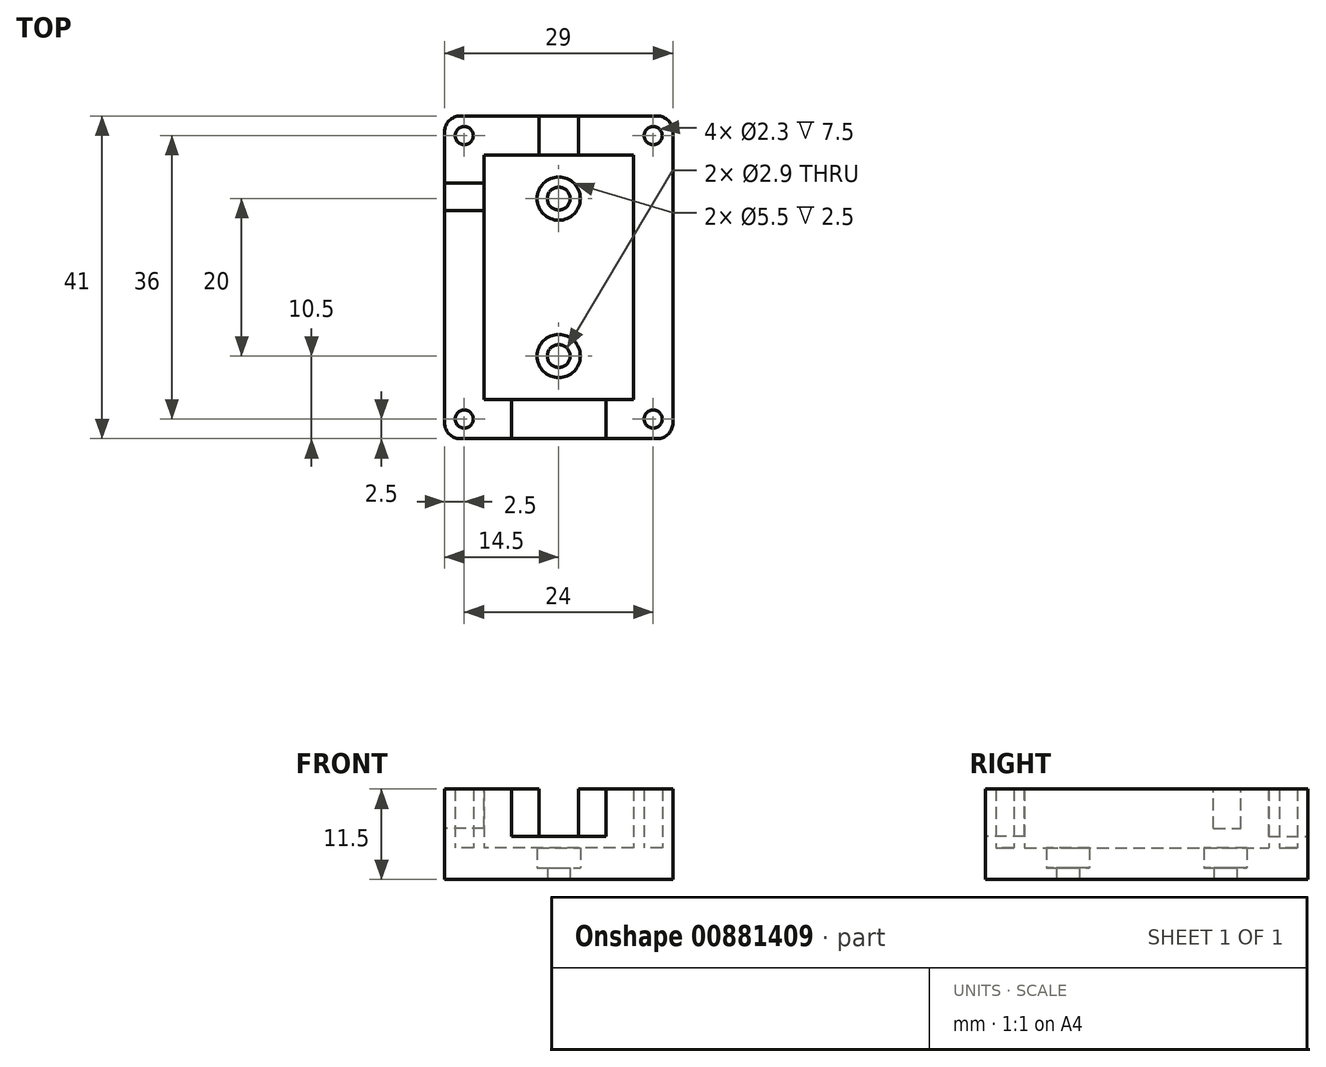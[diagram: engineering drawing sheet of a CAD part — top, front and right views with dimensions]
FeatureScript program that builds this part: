
annotation { "Feature Type Name" : "Feature", "Feature Type Description" : "" }
export const myFeature = defineFeature(function(context is Context, id is Id, definition is map)
    precondition{}
    {
        {
            var Q0;
            Q0=qCreatedBy(makeId("Top.planeOp"),FACE);
            var sketch = newSketch(context, id + "F0", { "sketchPlane" : qUnion([Q0])});
            skLineSegment(sketch, "E0.bottom", {"start": v(9.5, -15.5) * mm, "end": v(-9.5, -15.5) * mm});
            skLineSegment(sketch, "E0.top", {"start": v(9.5, 15.5) * mm, "end": v(-9.5, 15.5) * mm});
            skLineSegment(sketch, "E0.left", {"start": v(9.5, -15.5) * mm, "end": v(9.5, 15.5) * mm});
            skLineSegment(sketch, "E0.right", {"start": v(-9.5, -15.5) * mm, "end": v(-9.5, 15.5) * mm});
            skPoint(sketch, "E0.middle", {"position": v(0, 0) * mm});
            skLineSegment(sketch, "E1.0", {"start": v(14.5, 20.5) * mm, "end": v(-14.5, 20.5) * mm});
            skLineSegment(sketch, "E1.1", {"start": v(14.5, -20.5) * mm, "end": v(14.5, 20.5) * mm});
            skLineSegment(sketch, "E1.2", {"start": v(14.5, -20.5) * mm, "end": v(-14.5, -20.5) * mm});
            skLineSegment(sketch, "E1.3", {"start": v(-14.5, -20.5) * mm, "end": v(-14.5, 20.5) * mm});
            skPoint(sketch, "E2", {"position": v(12, 18) * mm});
            skPoint(sketch, "E3", {"position": v(-12, 18) * mm});
            skPoint(sketch, "E4", {"position": v(-12, -18) * mm});
            skPoint(sketch, "E5", {"position": v(12, -18) * mm});
            skCircle(sketch, "E6", {"center": v(-12, -18) * mm, "radius": 1.15 * mm});
            skCircle(sketch, "E7", {"center": v(12, -18) * mm, "radius": 1.15 * mm});
            skCircle(sketch, "E8", {"center": v(12, 18) * mm, "radius": 1.15 * mm});
            skCircle(sketch, "E9", {"center": v(-12, 18) * mm, "radius": 1.15 * mm});
            skSolve(sketch);
        }
        {
            var Q0;
            Q0=makeQuery(id+"F0.imprint","IMPRINT",FACE,{"disambiguationData":[TD([[makeQuery(id+"F0.imprint","IMPRINT",EDGE,{"derivedFrom":sQuery(id+"F0.wireOp",EDGE,"E0.bottom")}),1.0]])]});
            extrude(context, id + "F1", {"entities" : qUnion([Q0]), "depth" : 7.5 * mm, "offsetDistance" : 25 * mm});
        }
        {
            var Q0;
            Q0=makeQuery(id+"F1.opExtrude","CAP_FACE",FACE,{"disambiguationData":[OSD([sQuery(id+"F0.wireOp",EDGE,"E0.bottom"),sQuery(id+"F0.wireOp",EDGE,"E0.top"),sQuery(id+"F0.wireOp",EDGE,"E0.left"),sQuery(id+"F0.wireOp",EDGE,"E0.right"),sQuery(id+"F0.wireOp",EDGE,"E1.0"),sQuery(id+"F0.wireOp",EDGE,"E1.1"),sQuery(id+"F0.wireOp",EDGE,"E1.2"),sQuery(id+"F0.wireOp",EDGE,"E1.3"),sQuery(id+"F0.wireOp",EDGE,"E6"),sQuery(id+"F0.wireOp",EDGE,"E7"),sQuery(id+"F0.wireOp",EDGE,"E8"),sQuery(id+"F0.wireOp",EDGE,"E9")])],"isStart":true});
            var sketch = newSketch(context, id + "F2", { "sketchPlane" : qUnion([Q0])});
            skLineSegment(sketch, "E10.bottom", {"start": v(-14.5, 20.5) * mm, "end": v(14.5, 20.5) * mm});
            skLineSegment(sketch, "E10.top", {"start": v(-14.5, -20.5) * mm, "end": v(14.5, -20.5) * mm});
            skLineSegment(sketch, "E10.left", {"start": v(-14.5, 20.5) * mm, "end": v(-14.5, -20.5) * mm});
            skLineSegment(sketch, "E10.right", {"start": v(14.5, 20.5) * mm, "end": v(14.5, -20.5) * mm});
            skSolve(sketch);
        }
        {
            var Q0;
            Q0=makeQuery(id+"F2.imprint","IMPRINT",FACE,{"disambiguationData":[TD([[makeQuery(id+"F2.imprint","IMPRINT",EDGE,{"derivedFrom":sQuery(id+"F2.wireOp",EDGE,"E10.bottom")}),1.0]])]});
            var Q1;
            Q1=makeQuery(id+"F2.imprint","IMPRINT",FACE,{"disambiguationData":[TD([[makeQuery(id+"F2.imprint","IMPRINT",EDGE,{"derivedFrom":makeQuery(id+"F1.opExtrude","CAP_EDGE",EDGE,{"disambiguationData":[OSD([sQuery(id+"F0.wireOp",EDGE,"E0.bottom")])],"isStart":true})}),1.0]])]});
            var Q2;
            Q2=makeQuery(id+"F2.imprint","IMPRINT",FACE,{"disambiguationData":[TD([[makeQuery(id+"F2.imprint","IMPRINT",EDGE,{"derivedFrom":makeQuery(id+"F1.opExtrude","CAP_EDGE",EDGE,{"disambiguationData":[OSD([sQuery(id+"F0.wireOp",EDGE,"E7")])],"isStart":true})}),-1.0]])]});
            var Q3;
            Q3=makeQuery(id+"F2.imprint","IMPRINT",FACE,{"disambiguationData":[TD([[makeQuery(id+"F2.imprint","IMPRINT",EDGE,{"derivedFrom":makeQuery(id+"F1.opExtrude","CAP_EDGE",EDGE,{"disambiguationData":[OSD([sQuery(id+"F0.wireOp",EDGE,"E6")])],"isStart":true})}),-1.0]])]});
            var Q4;
            Q4=makeQuery(id+"F2.imprint","IMPRINT",FACE,{"disambiguationData":[TD([[makeQuery(id+"F2.imprint","IMPRINT",EDGE,{"derivedFrom":makeQuery(id+"F1.opExtrude","CAP_EDGE",EDGE,{"disambiguationData":[OSD([sQuery(id+"F0.wireOp",EDGE,"E9")])],"isStart":true})}),-1.0]])]});
            var Q5;
            Q5=makeQuery(id+"F2.imprint","IMPRINT",FACE,{"disambiguationData":[TD([[makeQuery(id+"F2.imprint","IMPRINT",EDGE,{"derivedFrom":makeQuery(id+"F1.opExtrude","CAP_EDGE",EDGE,{"disambiguationData":[OSD([sQuery(id+"F0.wireOp",EDGE,"E8")])],"isStart":true})}),-1.0]])]});
            extrude(context, id + "F3", {"entities" : qUnion([Q0, Q1, Q2, Q3, Q4, Q5]), "operationType" : NewBodyOperationType.ADD, "depth" : 4 * mm, "offsetDistance" : 25 * mm});
        }
        {
            var Q0;
            Q0=makeQuery(id+"F1.opExtrude","CAP_FACE",FACE,{"disambiguationData":[OSD([sQuery(id+"F0.wireOp",EDGE,"E0.bottom"),sQuery(id+"F0.wireOp",EDGE,"E0.top"),sQuery(id+"F0.wireOp",EDGE,"E0.left"),sQuery(id+"F0.wireOp",EDGE,"E0.right"),sQuery(id+"F0.wireOp",EDGE,"E1.0"),sQuery(id+"F0.wireOp",EDGE,"E1.1"),sQuery(id+"F0.wireOp",EDGE,"E1.2"),sQuery(id+"F0.wireOp",EDGE,"E1.3"),sQuery(id+"F0.wireOp",EDGE,"E6"),sQuery(id+"F0.wireOp",EDGE,"E7"),sQuery(id+"F0.wireOp",EDGE,"E8"),sQuery(id+"F0.wireOp",EDGE,"E9")])],"isStart":false});
            var sketch = newSketch(context, id + "F4", { "sketchPlane" : qUnion([Q0])});
            skPoint(sketch, "E11", {"position": v(6, -15.5) * mm});
            skPoint(sketch, "E12", {"position": v(6, -20.5) * mm});
            skPoint(sketch, "E13", {"position": v(-6, -15.5) * mm});
            skPoint(sketch, "E14", {"position": v(-6, -20.5) * mm});
            skLineSegment(sketch, "E15", {"start": v(-6, -15.5) * mm, "end": v(-6, -20.5) * mm});
            skLineSegment(sketch, "E16", {"start": v(6, -20.5) * mm, "end": v(6, -15.5) * mm});
            skPoint(sketch, "E17", {"position": v(2.5, 15.5) * mm});
            skPoint(sketch, "E18", {"position": v(-2.5, 15.5) * mm});
            skLineSegment(sketch, "E19", {"start": v(-2.5, 15.5) * mm, "end": v(-2.5, 20.5) * mm});
            skLineSegment(sketch, "E20", {"start": v(-2.5, 20.5) * mm, "end": v(2.5, 20.5) * mm});
            skLineSegment(sketch, "E21", {"start": v(2.5, 20.5) * mm, "end": v(2.5, 15.5) * mm});
            skSolve(sketch);
        }
        {
            var Q0;
            {var subQ0=sQuery(id+"F4.wireOp",EDGE,"E15");Q0=makeQuery(id+"F4.imprint","IMPRINT",FACE,{"disambiguationData":[TD([[makeQuery(id+"F4.imprint","IMPRINT",EDGE,{"derivedFrom":subQ0}),1.0]])]});}
            var Q1;
            {var subQ0=sQuery(id+"F4.wireOp",EDGE,"E19");Q1=makeQuery(id+"F4.imprint","IMPRINT",FACE,{"disambiguationData":[TD([[makeQuery(id+"F4.imprint","IMPRINT",EDGE,{"derivedFrom":subQ0}),-1.0]])]});}
            extrude(context, id + "F5", {"entities" : qUnion([Q0, Q1]), "operationType" : NewBodyOperationType.REMOVE, "oppositeDirection" : true, "depth" : 6 * mm, "offsetDistance" : 25 * mm});
        }
        {
            var Q0;
            Q0=makeQuery(id+"F3.boolean.opBoolean","MERGE",EDGE,{"derivedFrom":[makeQuery(id+"F1.opExtrude","SWEPT_EDGE",EDGE,{"disambiguationData":[OSD([sQuery(id+"F0.wireOp",EDGE,"E1.0"),sQuery(id+"F0.wireOp",EDGE,"E1.3")])]}),makeQuery(id+"F3.opExtrude","SWEPT_EDGE",EDGE,{"disambiguationData":[OSD([sQuery(id+"F2.wireOp",EDGE,"E10.top"),sQuery(id+"F2.wireOp",EDGE,"E10.left")])]})]});
            var Q1;
            Q1=makeQuery(id+"F3.boolean.opBoolean","MERGE",EDGE,{"derivedFrom":[makeQuery(id+"F1.opExtrude","SWEPT_EDGE",EDGE,{"disambiguationData":[OSD([sQuery(id+"F0.wireOp",EDGE,"E1.0"),sQuery(id+"F0.wireOp",EDGE,"E1.1")])]}),makeQuery(id+"F3.opExtrude","SWEPT_EDGE",EDGE,{"disambiguationData":[OSD([sQuery(id+"F2.wireOp",EDGE,"E10.top"),sQuery(id+"F2.wireOp",EDGE,"E10.right")])]})]});
            var Q2;
            Q2=makeQuery(id+"F3.boolean.opBoolean","MERGE",EDGE,{"derivedFrom":[makeQuery(id+"F1.opExtrude","SWEPT_EDGE",EDGE,{"disambiguationData":[OSD([sQuery(id+"F0.wireOp",EDGE,"E1.1"),sQuery(id+"F0.wireOp",EDGE,"E1.2")])]}),makeQuery(id+"F3.opExtrude","SWEPT_EDGE",EDGE,{"disambiguationData":[OSD([sQuery(id+"F2.wireOp",EDGE,"E10.bottom"),sQuery(id+"F2.wireOp",EDGE,"E10.right")])]})]});
            var Q3;
            Q3=makeQuery(id+"F3.boolean.opBoolean","MERGE",EDGE,{"derivedFrom":[makeQuery(id+"F1.opExtrude","SWEPT_EDGE",EDGE,{"disambiguationData":[OSD([sQuery(id+"F0.wireOp",EDGE,"E1.2"),sQuery(id+"F0.wireOp",EDGE,"E1.3")])]}),makeQuery(id+"F3.opExtrude","SWEPT_EDGE",EDGE,{"disambiguationData":[OSD([sQuery(id+"F2.wireOp",EDGE,"E10.bottom"),sQuery(id+"F2.wireOp",EDGE,"E10.left")])]})]});
            fillet(context, id + "F6", {"entities" : qUnion([Q0, Q1, Q2, Q3]), "tangentPropagation" : true, "radius" : 2 * mm, "defaultsChanged" : false, "vertexSettings" : [], "allowEdgeOverflow" : false});
        }
        {
            var Q0;
            Q0=makeQuery(id+"F3.boolean.opBoolean","SPLIT",FACE,{"disambiguationData":[TD([makeQuery(id+"F1.opExtrude","SWEPT_FACE",FACE,{"disambiguationData":[OSD([sQuery(id+"F0.wireOp",EDGE,"E0.bottom")])]})])],"derivedFrom":makeQuery(id+"F3.opExtrude","CAP_FACE",FACE,{"disambiguationData":[OSD([sQuery(id+"F2.wireOp",EDGE,"E10.bottom"),sQuery(id+"F2.wireOp",EDGE,"E10.top"),sQuery(id+"F2.wireOp",EDGE,"E10.left"),sQuery(id+"F2.wireOp",EDGE,"E10.right")])],"isStart":true})});
            var sketch = newSketch(context, id + "F7", { "sketchPlane" : qUnion([Q0])});
            skPoint(sketch, "E22", {"position": v(0, 10) * mm});
            skPoint(sketch, "E23", {"position": v(0, -10) * mm});
            skSolve(sketch);
        }
        {
            var Q0;
            Q0=sQuery(id+"F7.wireOp",VERTEX,"E22");
            var Q1;
            Q1=sQuery(id+"F7.wireOp",VERTEX,"E23");
            var Q2;
            Q2=makeQuery(id+"F1.opExtrude","SWEPT_BODY",BODY,{"disambiguationData":[OSD([sQuery(id+"F0.wireOp",EDGE,"E0.bottom"),sQuery(id+"F0.wireOp",EDGE,"E0.top"),sQuery(id+"F0.wireOp",EDGE,"E0.left"),sQuery(id+"F0.wireOp",EDGE,"E0.right"),sQuery(id+"F0.wireOp",EDGE,"E1.0"),sQuery(id+"F0.wireOp",EDGE,"E1.1"),sQuery(id+"F0.wireOp",EDGE,"E1.2"),sQuery(id+"F0.wireOp",EDGE,"E1.3"),sQuery(id+"F0.wireOp",EDGE,"E6"),sQuery(id+"F0.wireOp",EDGE,"E7"),sQuery(id+"F0.wireOp",EDGE,"E8"),sQuery(id+"F0.wireOp",EDGE,"E9")])]});
            hole(context, id + "F8", {"style" : HoleStyle.C_BORE, "endStyle" : HoleEndStyle.THROUGH, "standardTappedOrClearance" : lookupTablePath({ "fit" : "Normal", "standard" : "ISO", "size" : "M2.5", "type" : "Clearance" }), "standardBlindInLast" : lookupTablePath({ "fit" : "Normal", "standard" : "ISO", "engagement" : "75%", "pitch" : "0.35 mm", "size" : "M2.5", "type" : "Clearance & tapped" }), "holeDiameter" : 2.9 * mm, "cBoreDiameter" : 5.5 * mm, "cBoreDepth" : 2.5 * mm, "majorDiameter" : 5 * mm, "isTappedThrough" : true, "tappedDepth" : 12 * mm, "tapClearance" : 3, "locations" : qUnion([Q0, Q1]), "scope" : qUnion([Q2]), "startStyle" : HoleStartStyle.SKETCH});
        }
        {
            var Q0;
            {var subQ0=sQuery(id+"F0.wireOp",EDGE,"E9");var subQ1=sQuery(id+"F0.wireOp",EDGE,"E6");var subQ2=sQuery(id+"F0.wireOp",EDGE,"E1.3");var subQ3=sQuery(id+"F0.wireOp",EDGE,"E1.2");var subQ4=sQuery(id+"F0.wireOp",EDGE,"E0.bottom");var subQ5=sQuery(id+"F0.wireOp",EDGE,"E0.right");var subQ6=sQuery(id+"F0.wireOp",EDGE,"E0.top");var subQ7=sQuery(id+"F0.wireOp",EDGE,"E1.0");Q0=makeQuery(id+"F5.boolean.opBoolean","SPLIT",FACE,{"disambiguationData":[TD([makeQuery(id+"F1.opExtrude","SWEPT_FACE",FACE,{"disambiguationData":[OSD([subQ5])]})])],"derivedFrom":makeQuery(id+"F1.opExtrude","CAP_FACE",FACE,{"disambiguationData":[OSD([subQ4,subQ6,sQuery(id+"F0.wireOp",EDGE,"E0.left"),subQ5,subQ7,sQuery(id+"F0.wireOp",EDGE,"E1.1"),subQ3,subQ2,subQ1,sQuery(id+"F0.wireOp",EDGE,"E7"),sQuery(id+"F0.wireOp",EDGE,"E8"),subQ0])],"isStart":false})});}
            var sketch = newSketch(context, id + "F9", { "sketchPlane" : qUnion([Q0])});
            skPoint(sketch, "E24", {"position": v(-9.5, 15.5) * mm});
            skPoint(sketch, "E25", {"position": v(-9.5, 12) * mm});
            skPoint(sketch, "E26", {"position": v(-9.5, 8.5) * mm});
            skPoint(sketch, "E27", {"position": v(-14.5, 8.5) * mm});
            skPoint(sketch, "E28", {"position": v(-14.5, 12) * mm});
            skLineSegment(sketch, "E29", {"start": v(-9.5, 12) * mm, "end": v(-9.5, 8.5) * mm});
            skLineSegment(sketch, "E30", {"start": v(-14.5, 8.5) * mm, "end": v(-14.5, 12) * mm});
            skLineSegment(sketch, "E31", {"start": v(-9.5, 12) * mm, "end": v(-14.5, 12) * mm});
            skLineSegment(sketch, "E32", {"start": v(-14.5, 8.5) * mm, "end": v(-9.5, 8.5) * mm});
            skSolve(sketch);
        }
        {
            var Q0;
            Q0=makeQuery(id+"F9.imprint","IMPRINT",FACE,{"disambiguationData":[TD([[makeQuery(id+"F9.imprint","IMPRINT",EDGE,{"derivedFrom":sQuery(id+"F9.wireOp",EDGE,"E29")}),1.0]])]});
            extrude(context, id + "F10", {"entities" : qUnion([Q0]), "operationType" : NewBodyOperationType.REMOVE, "oppositeDirection" : true, "depth" : 5 * mm, "offsetDistance" : 25 * mm});
        }
    });
